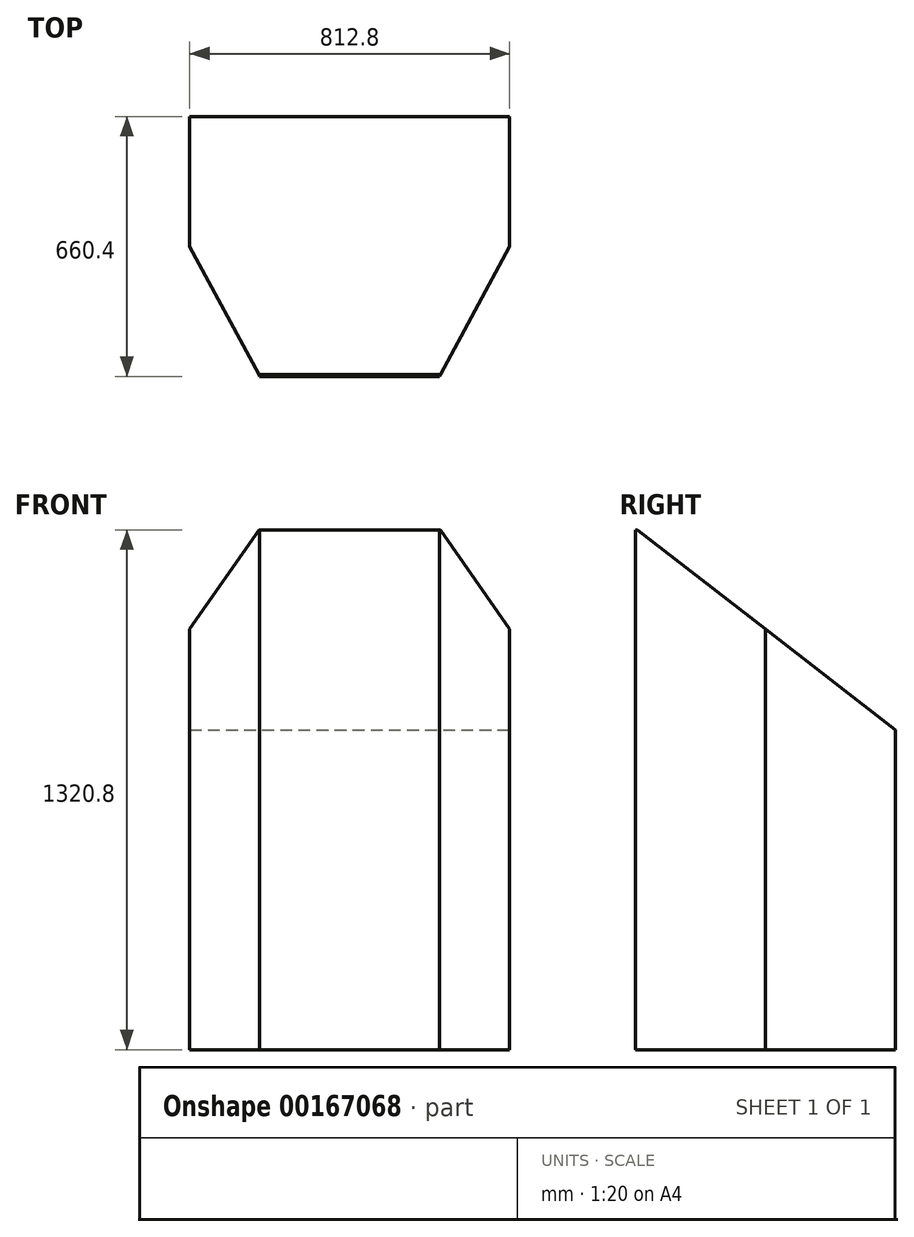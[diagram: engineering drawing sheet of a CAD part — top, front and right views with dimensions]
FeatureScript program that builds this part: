
annotation { "Feature Type Name" : "Feature", "Feature Type Description" : "" }
export const myFeature = defineFeature(function(context is Context, id is Id, definition is map)
    precondition{}
    {
        {
            var Q0;
            Q0=qCreatedBy(makeId("Top.planeOp"),FACE);
            var sketch = newSketch(context, id + "F0", { "sketchPlane" : qUnion([Q0])});
            skLineSegment(sketch, "E0.bottom", {"start": v(0, 0) * mm, "end": v(812.8, 0) * mm});
            skLineSegment(sketch, "E0.top", {"start": v(177.8, -660.4) * mm, "end": v(635, -660.4) * mm});
            skLineSegment(sketch, "E0.left", {"start": v(0, 0) * mm, "end": v(0, -330.2) * mm});
            skLineSegment(sketch, "E0.right", {"start": v(812.8, 0) * mm, "end": v(812.8, -330.2) * mm});
            skLineSegment(sketch, "E1", {"start": v(0, -330.2) * mm, "end": v(177.8, -660.4) * mm});
            skLineSegment(sketch, "E2", {"start": v(812.8, -330.2) * mm, "end": v(635, -660.4) * mm});
            skPoint(sketch, "E3.orphan", {"position": v(812.8, -660.4) * mm});
            skSolve(sketch);
        }
        {
            var Q0;
            Q0 = qSketchRegion(id + "F0", true);
            extrude(context, id + "F1", {"entities" : qUnion([Q0]), "depth" : 1320.8 * mm});
        }
        {
            var Q0;
            Q0=makeQuery(id+"F1.opExtrude","SWEPT_FACE",FACE,{"disambiguationData":[OSD([sQuery(id+"F0.wireOp",EDGE,"E0.right")])]});
            var sketch = newSketch(context, id + "F2", { "sketchPlane" : qUnion([Q0])});
            skLineSegment(sketch, "E4", {"start": v(-660.4, 1323.8) * mm, "end": v(0, 1320.8) * mm});
            skLineSegment(sketch, "E5", {"start": v(0, 1320.8) * mm, "end": v(0, 812.8) * mm});
            skLineSegment(sketch, "E6", {"start": v(0, 812.8) * mm, "end": v(-660.4, 1323.8) * mm});
            skSolve(sketch);
        }
        {
            var Q0;
            Q0 = qSketchRegion(id + "F2", true);
            extrude(context, id + "F3", {"entities" : qUnion([Q0]), "operationType" : NewBodyOperationType.REMOVE, "endBound" : BoundingType.THROUGH_ALL, "oppositeDirection" : true, "depth" : 25.4 * mm});
        }
    });
